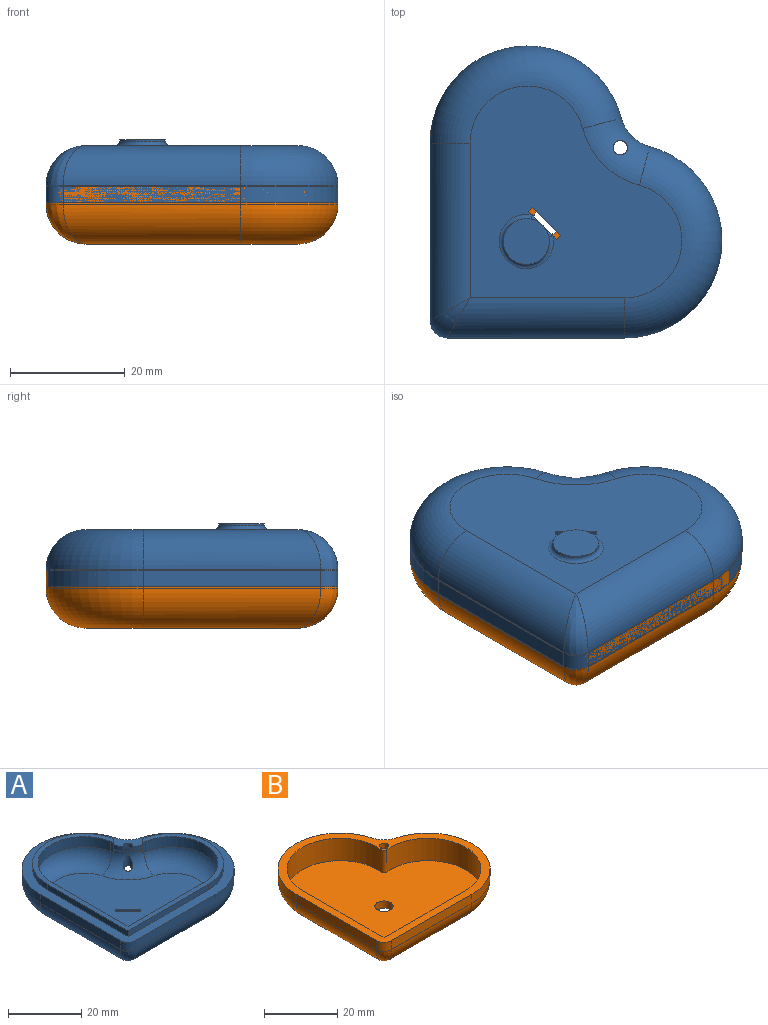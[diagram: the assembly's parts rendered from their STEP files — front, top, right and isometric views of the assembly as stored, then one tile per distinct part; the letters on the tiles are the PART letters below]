
ASSEMBLY  parts=2 mates=1
PART A: 52 faces, bbox 53.8x53.8x13.3 mm
  f0: cylinder r=8.5mm len=3.4mm, axis (0,0,1), area 3.4mm2, adj f11,f23,f24,f43
  f1: plane 37x37mm, normal (0,0,-1), area 944.2mm2, adj f12,f13,f14,f15,f16,f35,f36,f37
  f2: cylinder r=17mm len=33.43mm, axis (0,0,-1), area 146.9mm2, adj f3,f6,f14,f17
  f3: plane 31x3mm, normal (-1,0,0), area 93mm2, adj f2,f6,f12,f41
  f4: plane 31x3mm, normal (0,-1,0), area 93mm2, adj f5,f6,f13,f41
  f5: cylinder r=17mm len=33.43mm, axis (0,0,-1), area 146.9mm2, adj f4,f6,f15,f17
  f6: plane 51x51mm, normal (0,0,1), area 471.9mm2, adj f2,f3,f4,f5,f7,f8,f9,f10
  f7: cylinder r=14.1mm len=27.97mm, axis (0,0,-1), area 79.4mm2, adj f6,f8,f11,f43
  f8: plane 31.1x1.9mm, normal (-1,0,0), area 59.1mm2, adj f6,f7,f9,f11
  f9: plane 31.1x1.9mm, normal (0,-1,0), area 59.1mm2, adj f6,f8,f10,f11
  f10: cylinder r=14.1mm len=27.97mm, axis (0,0,-1), area 79.4mm2, adj f6,f9,f11,f45
  f11: plane 45.2x45.2mm, normal (0,0,1), area 211.2mm2, adj f0,f7,f8,f9,f10,f24,f25,f26
  f12: cylinder r=7mm len=31mm, axis (0,-1,0), area 324.9mm2, adj f1,f3,f14,f42
  f13: cylinder r=7mm len=31mm, axis (1,0,0), area 324.9mm2, adj f1,f4,f15,f42
  f14: torus R=10mm, axis (0,0,1), area 457.9mm2, adj f1,f2,f12,f16
  f15: torus R=10mm, axis (0,0,1), area 457.9mm2, adj f1,f5,f13,f16
  f16: torus R=14mm, axis (0,0,1), area 103.9mm2, adj f1,f14,f15,f17,f39
  f17: cylinder r=7mm len=4.96mm, axis (0,0,1), area 22mm2, adj f2,f5,f6,f16
  f18: plane 37x37mm, normal (0,0,1), area 1012.5mm2, adj f29,f30,f31,f32,f33,f35,f36,f37
  f19: cylinder r=15.5mm len=30.48mm, axis (0,0,-1), area 67mm2, adj f20,f23,f31,f34
  f20: plane 32.5x1.5mm, normal (1,0,0), area 48.8mm2, adj f19,f21,f23,f29
  f21: plane 32.5x1.5mm, normal (0,1,0), area 48.8mm2, adj f20,f22,f23,f30
  f22: cylinder r=15.5mm len=30.48mm, axis (0,0,-1), area 67mm2, adj f21,f23,f32,f34
  f23: plane 48x48mm, normal (0,0,-1), area 432.6mm2, adj f0,f19,f20,f21,f22,f24,f25,f26
  f24: cylinder r=12.6mm len=25mm, axis (0,0,-1), area 126.9mm2, adj f0,f11,f23,f25
  f25: plane 29.6x3.4mm, normal (1,0,0), area 100.6mm2, adj f11,f23,f24,f26
  f26: plane 29.6x3.4mm, normal (0,1,0), area 100.6mm2, adj f11,f23,f25,f27
  f27: cylinder r=12.6mm len=25mm, axis (0,0,-1), area 126.9mm2, adj f11,f23,f26,f28
  f28: cylinder r=8.5mm len=3.4mm, axis (0,0,1), area 3.4mm2, adj f11,f23,f27,f45
  f29: cylinder r=5.5mm len=32.5mm, axis (0,-1,0), area 263.5mm2, adj f18,f20,f30,f31
  f30: cylinder r=5.5mm len=32.5mm, axis (1,0,0), area 263.5mm2, adj f18,f21,f29,f32
  f31: torus R=10mm, axis (0,0,1), area 336mm2, adj f18,f19,f29,f33
  f32: torus R=10mm, axis (0,0,1), area 336mm2, adj f18,f22,f30,f33
  f33: torus R=14mm, axis (0,0,1), area 86.7mm2, adj f18,f31,f32,f34,f39
  f34: cylinder r=8.5mm len=6.02mm, axis (0,0,1), area 13.4mm2, adj f19,f22,f23,f33
  f35: plane 4.95x4.95mm, normal (-0.71,-0.71,0), area 10.5mm2, adj f1,f18,f36,f38
  f36: plane 1.5x0.71mm, normal (-0.71,0.71,0), area 1.5mm2, adj f1,f18,f35,f37
  f37: plane 4.95x4.95mm, normal (0.71,0.71,0), area 10.5mm2, adj f1,f18,f36,f38,f49,f51
  f38: plane 1.5x0.71mm, normal (0.71,-0.71,0), area 1.5mm2, adj f1,f18,f35,f37
  f39: cylinder r=1.25mm len=5.42mm, axis (0,0,1), area 17.6mm2, adj f16,f33
  f40: cylinder r=1.25mm len=2.42mm, axis (0,0,1), area 7.5mm2, adj f6,f23,f44,f46
  f41: cylinder r=3mm len=3mm, axis (0,0,-1), area 14.1mm2, adj f3,f4,f6,f42
  f42: bspline ~8.3x7mm, area 34.9mm2, adj f12,f13,f41
  f43: plane 3.4x1.24mm, normal (0.71,-0.71,0), area 6mm2, adj f0,f7,f11,f23,f44
  f44: cylinder r=7mm len=2.83mm, axis (0,0,1), area 4.6mm2, adj f6,f23,f40,f43
  f45: plane 3.4x1.24mm, normal (-0.71,0.71,0), area 6mm2, adj f10,f11,f23,f28,f46
  f46: cylinder r=7mm len=2.83mm, axis (0,0,1), area 4.6mm2, adj f6,f23,f40,f45
  f47: cylinder r=4mm len=8mm, axis (0,0,1), area 8mm2, adj f48,f49,f50,f51
  f48: plane 8x8mm, normal (0,0,-1), area 50.3mm2, adj f47
  f49: bspline ~2.23x1.99mm, area 1.2mm2, adj f37,f47,f50
  f50: torus R=4.75mm, axis (0,0,1), area 25.9mm2, adj f1,f47,f49,f51
  f51: bspline ~2.23x1.99mm, area 1.2mm2, adj f37,f47,f50
PART B: 22 faces, bbox 53.8x53.8x12 mm
  f0: plane 37x37mm, normal (0,0,-1), area 999.8mm2, adj f11,f12,f13,f14,f15,f19
  f1: cylinder r=17mm len=33.43mm, axis (0,0,-1), area 146.9mm2, adj f2,f5,f13,f16
  f2: plane 31x3mm, normal (-1,0,0), area 93mm2, adj f1,f5,f11,f17
  f3: plane 31x3mm, normal (0,-1,0), area 93mm2, adj f4,f5,f12,f17
  f4: cylinder r=17mm len=33.43mm, axis (0,0,-1), area 146.9mm2, adj f3,f5,f14,f16
  f5: plane 51x51mm, normal (0,0,1), area 414.7mm2, adj f1,f2,f3,f4,f6,f7,f8,f9
  f6: cylinder r=14.5mm len=29mm, axis (0,0,-1), area 352.8mm2, adj f5,f7,f10,f21
  f7: plane 31.5x7.5mm, normal (1,0,0), area 236.2mm2, adj f5,f6,f8,f10
  f8: plane 31.5x7.5mm, normal (0,1,0), area 236.2mm2, adj f5,f7,f9,f10
  f9: cylinder r=14.5mm len=29mm, axis (0,0,-1), area 352.8mm2, adj f5,f8,f10,f21
  f10: plane 46x46mm, normal (0,0,1), area 1626.9mm2, adj f6,f7,f8,f9,f19,f21
  f11: cylinder r=7mm len=31mm, axis (0,-1,0), area 324.9mm2, adj f0,f2,f13,f18
  f12: cylinder r=7mm len=31mm, axis (1,0,0), area 324.9mm2, adj f0,f3,f14,f18
  f13: torus R=10mm, axis (0,0,1), area 457.9mm2, adj f0,f1,f11,f15
  f14: torus R=10mm, axis (0,0,1), area 457.9mm2, adj f0,f4,f12,f15
  f15: torus R=14mm, axis (0,0,1), area 103.9mm2, adj f0,f13,f14,f16,f20
  f16: cylinder r=7mm len=4.96mm, axis (0,0,1), area 22mm2, adj f1,f4,f5,f15
  f17: cylinder r=3mm len=3mm, axis (0,0,-1), area 14.1mm2, adj f2,f3,f5,f18
  f18: bspline ~8.3x7mm, area 34.9mm2, adj f11,f12,f17
  f19: cylinder r=2.5mm len=5mm, axis (0,0,-1), area 39.3mm2, adj f0,f10
  f20: cylinder r=1.25mm len=9.36mm, axis (0,0,1), area 67.1mm2, adj f5,f15
  f21: cylinder r=1mm len=7.5mm, axis (0,0,-1), area 13.3mm2, adj f5,f6,f9,f10
PLACE A rot(axis=(0.71,0.71,0),180deg) t=(-18.54,-43.83,5.28)mm
PLACE B t=(-18.54,-43.83,-11.92)mm
MATE fastened A.f5 <-> B.f1  axis (0,0,1) through (-18.54,-26.83,-5.67)mm
